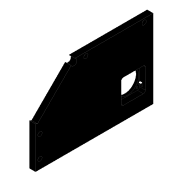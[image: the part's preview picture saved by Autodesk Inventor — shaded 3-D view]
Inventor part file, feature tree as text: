
AUTODESK INVENTOR PART (.ipt)
format: ipt  version: 2020 (Build 240168000, 168)  size: 358,912 bytes
history: native  units: mm
features: extrude x10, sketch x10, chamfer x4, fillet x3, projected_geometry x3
ambient origin geometry x8: Origin, YZ Plane, XZ Plane, XY Plane, X Axis, Y Axis, Z Axis, Center Point
bodies: Solid1 (feature_tree)
feature tree (30):
  extrude  "Extrusion1"  Depth=4.5mm
  extrude  "Extrusion2"  Depth=4.5mm
  extrude  "Extrusion3"  Depth=7.1mm
  chamfer  "Chamfer1"  Distance=4.5mm
  chamfer  "Chamfer2"  Distance=181.0mm
  extrude  "Extrusion4"  Depth=2.0mm TaperAngle=45.0deg
  extrude  "Extrusion5"  Depth=3.0mm
  extrude  "Extrusion6"  Depth=3.0mm TaperAngle=0.0deg
  extrude  "Extrusion7"  Depth=3.0mm
  extrude  "Extrusion8"  Depth=3.0mm
  fillet  "Fillet1"  Radius=3.0mm
  extrude  "Extrusion9"  Depth=3.0mm
  extrude  "Extrusion10"  Depth=3.0mm
  fillet  "Fillet2"  Radius=23.0mm
  fillet  "Fillet3"  Radius=13.0mm
  chamfer  "Chamfer3"  Distance=0.2mm
  chamfer  "Chamfer4"  Distance=3.5mm
  sketch  "Sketch1"  dims[d1=4.5mm d2=4.5mm]
  sketch  "Sketch2"  dims[d3=4.5mm d4=4.5mm]
  sketch  "Sketch3"  dims[d5=9.9mm d6=0.0mm d7=7.1mm]
  sketch  "Sketch4"  dims[d8=7.1mm]
  sketch  "Sketch5"  dims[d9=7.1mm]
  projected_geometry  "Projected Loop1"
  projected_geometry  "Projected Loop2"
  sketch  "Sketch6"  dims[d10=7.1mm d11=4.5mm d12=0.0mm]
  sketch  "Sketch7"  dims[d13=5.0mm]
  sketch  "Sketch8"  dims[d14=5.5mm]
  projected_geometry  "Projected Loop3"
  sketch  "Sketch10"  dims[d15=3.25mm d16=181.0mm d17=0.0mm]
  sketch  "Sketch11"  dims[d18=2.0mm d19=4.0mm d20=45.0deg d21=2.0mm d22=4.0mm d23=45.0deg d24=6.0mm d25=6.0mm d26=3.054mm d27=26.946mm d28=4.0mm d29=0.0mm d30=4.2mm d31=4.2mm d32=3.0mm d33=0.0mm d34=40.0mm d35=40.0mm d36=23.0mm d37=13.0mm d38=0.2mm d39=3.5mm d40=0.0mm d41=0.0mm d42=38.0mm d43=32.0mm d44=32.0mm d45=0.0mm d46=0.0mm d47=3.5mm d48=40.0mm d50=360.0deg d52=5.0mm d53=2.0mm d54=0.0mm d55=5.6mm d56=2.5mm d57=0.0mm d58=0.5mm d59=6.5mm d60=4.5mm d61=4.5mm d62=5.0mm d63=0.0mm d64=9.9mm d65=0.0mm d66=1.0mm d67=3.0mm d68=1.0mm d69=4.0mm d70=45.0deg d71=3.0mm d72=4.0mm d73=45.0deg]
